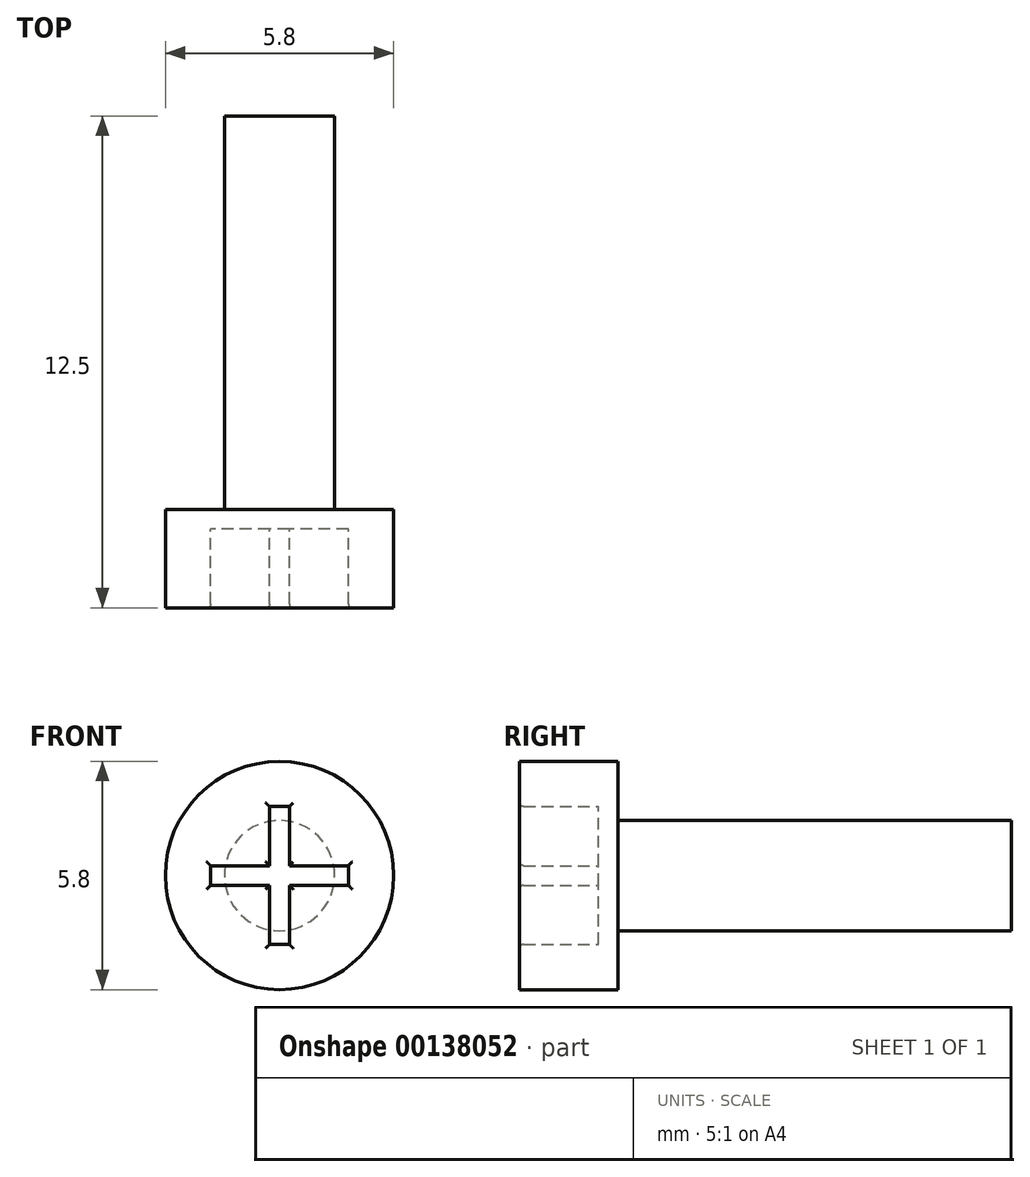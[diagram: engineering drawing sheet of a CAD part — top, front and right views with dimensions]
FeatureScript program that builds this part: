
annotation { "Feature Type Name" : "Feature", "Feature Type Description" : "" }
export const myFeature = defineFeature(function(context is Context, id is Id, definition is map)
    precondition{}
    {
        {
            var Q0;
            Q0=qCreatedBy(makeId("Front.planeOp"),FACE);
            var sketch = newSketch(context, id + "F0", { "sketchPlane" : qUnion([Q0])});
            skCircle(sketch, "E0", {"center": v(0, 0) * mm, "radius": 1.4 * mm});
            skSolve(sketch);
        }
        {
            var Q0;
            Q0=makeQuery(id+"F0.imprint","IMPRINT",FACE,{"disambiguationData":[TD([[makeQuery(id+"F0.imprint","IMPRINT",EDGE,{"derivedFrom":sQuery(id+"F0.wireOp",EDGE,"E0")}),1.0]])]});
            extrude(context, id + "F1", {"entities" : qUnion([Q0]), "depth" : 10 * mm});
        }
        {
            var Q0;
            Q0=makeQuery(id+"F1.opExtrude","CAP_FACE",FACE,{"disambiguationData":[OSD([sQuery(id+"F0.wireOp",EDGE,"E0")])],"isStart":false});
            cPlane(context, id + "F2", {"entities" : qUnion([Q0]), "cplaneType" : CPlaneType.OFFSET, "offset" : 0 * mm, "width" : 150 * mm, "height" : 150 * mm});
        }
        {
            var Q0;
            Q0=qCreatedBy(id+"F2.planeOp",FACE);
            var sketch = newSketch(context, id + "F3", { "sketchPlane" : qUnion([Q0])});
            skCircle(sketch, "E1", {"center": v(0, 0) * mm, "radius": 2.9 * mm});
            skLineSegment(sketch, "E2.bottom", {"start": v(0.25, -1.75) * mm, "end": v(-0.25, -1.75) * mm});
            skLineSegment(sketch, "E2.top", {"start": v(0.25, 1.75) * mm, "end": v(-0.25, 1.75) * mm});
            skLineSegment(sketch, "E2.left", {"start": v(0.25, -1.75) * mm, "end": v(0.25, 1.75) * mm});
            skLineSegment(sketch, "E2.right", {"start": v(-0.25, -1.75) * mm, "end": v(-0.25, 1.75) * mm});
            skLineSegment(sketch, "E3.bottom", {"start": v(1.75, -0.25) * mm, "end": v(-1.75, -0.25) * mm});
            skLineSegment(sketch, "E3.top", {"start": v(1.75, 0.25) * mm, "end": v(-1.75, 0.25) * mm});
            skLineSegment(sketch, "E3.left", {"start": v(1.75, -0.25) * mm, "end": v(1.75, 0.25) * mm});
            skLineSegment(sketch, "E3.right", {"start": v(-1.75, -0.25) * mm, "end": v(-1.75, 0.25) * mm});
            skSolve(sketch);
        }
        {
            var Q0;
            Q0=makeQuery(id+"F3.imprint","IMPRINT",FACE,{"disambiguationData":[TD([[makeQuery(id+"F3.imprint","IMPRINT",EDGE,{"derivedFrom":sQuery(id+"F3.wireOp",EDGE,"E1")}),1.0]])]});
            extrude(context, id + "F4", {"entities" : qUnion([Q0]), "operationType" : NewBodyOperationType.ADD, "depth" : 2.5 * mm});
        }
        {
            var Q0;
            {var subQ0=sQuery(id+"F3.wireOp",EDGE,"E3.bottom");var subQ1=sQuery(id+"F3.wireOp",EDGE,"E2.left");var subQ2=makeQuery(id+"F3.imprint","INTERSECT",VERTEX,{"derivedFrom":[subQ1,subQ0]});Q0=makeQuery(id+"F3.imprint","IMPRINT",FACE,{"disambiguationData":[TD([[makeQuery(id+"F3.imprint","IMPRINT",EDGE,{"disambiguationData":[TD([[subQ2,-1.0]])],"derivedFrom":subQ1}),1.0]])]});}
            var Q1;
            {var subQ5=sQuery(id+"F3.wireOp",EDGE,"E3.right");Q1=makeQuery(id+"F3.imprint","IMPRINT",FACE,{"disambiguationData":[TD([[makeQuery(id+"F3.imprint","IMPRINT",EDGE,{"derivedFrom":subQ5}),-1.0]])]});}
            var Q2;
            {var subQ0=sQuery(id+"F3.wireOp",EDGE,"E2.bottom");Q2=makeQuery(id+"F3.imprint","IMPRINT",FACE,{"disambiguationData":[TD([[makeQuery(id+"F3.imprint","IMPRINT",EDGE,{"derivedFrom":subQ0}),-1.0]])]});}
            var Q3;
            {var subQ5=sQuery(id+"F3.wireOp",EDGE,"E3.left");Q3=makeQuery(id+"F3.imprint","IMPRINT",FACE,{"disambiguationData":[TD([[makeQuery(id+"F3.imprint","IMPRINT",EDGE,{"derivedFrom":subQ5}),1.0]])]});}
            var Q4;
            {var subQ0=sQuery(id+"F3.wireOp",EDGE,"E2.top");Q4=makeQuery(id+"F3.imprint","IMPRINT",FACE,{"disambiguationData":[TD([[makeQuery(id+"F3.imprint","IMPRINT",EDGE,{"derivedFrom":subQ0}),1.0]])]});}
            extrude(context, id + "F5", {"entities" : qUnion([Q0, Q1, Q2, Q3, Q4]), "operationType" : NewBodyOperationType.ADD, "depth" : 0.5 * mm});
        }
        {
            var Q0;
            {var subQ0=sQuery(id+"F3.wireOp",EDGE,"E2.right");Q0=makeQuery(id+"F4.opExtrude","CAP_EDGE",EDGE,{"disambiguationData":[OSD([subQ0]),TDD([makeQuery(id+"F3.imprint","IMPRINT",EDGE,{"disambiguationData":[TD([[makeQuery(id+"F3.imprint","INTERSECT",VERTEX,{"derivedFrom":[sQuery(id+"F3.wireOp",EDGE,"E2.top"),subQ0]}),1.0]])],"derivedFrom":subQ0})])],"isStart":false});}
            var Q1;
            {var subQ0=sQuery(id+"F3.wireOp",EDGE,"E3.top");Q1=makeQuery(id+"F4.opExtrude","CAP_EDGE",EDGE,{"disambiguationData":[OSD([subQ0]),TDD([makeQuery(id+"F3.imprint","IMPRINT",EDGE,{"disambiguationData":[TD([[makeQuery(id+"F3.imprint","INTERSECT",VERTEX,{"derivedFrom":[subQ0,sQuery(id+"F3.wireOp",EDGE,"E3.right")]}),1.0]])],"derivedFrom":subQ0})])],"isStart":false});}
            var Q2;
            {var subQ0=sQuery(id+"F3.wireOp",EDGE,"E3.bottom");Q2=makeQuery(id+"F4.opExtrude","CAP_EDGE",EDGE,{"disambiguationData":[OSD([subQ0]),TDD([makeQuery(id+"F3.imprint","IMPRINT",EDGE,{"disambiguationData":[TD([[makeQuery(id+"F3.imprint","INTERSECT",VERTEX,{"derivedFrom":[subQ0,sQuery(id+"F3.wireOp",EDGE,"E3.right")]}),1.0]])],"derivedFrom":subQ0})])],"isStart":false});}
            var Q3;
            {var subQ0=sQuery(id+"F3.wireOp",EDGE,"E2.right");Q3=makeQuery(id+"F4.opExtrude","CAP_EDGE",EDGE,{"disambiguationData":[OSD([subQ0]),TDD([makeQuery(id+"F3.imprint","IMPRINT",EDGE,{"disambiguationData":[TD([[makeQuery(id+"F3.imprint","INTERSECT",VERTEX,{"derivedFrom":[sQuery(id+"F3.wireOp",EDGE,"E2.bottom"),subQ0]}),-1.0]])],"derivedFrom":subQ0})])],"isStart":false});}
            var Q4;
            Q4=makeQuery(id+"F4.opExtrude","CAP_EDGE",EDGE,{"disambiguationData":[OSD([sQuery(id+"F3.wireOp",EDGE,"E3.right")])],"isStart":false});
            var Q5;
            {var subQ0=sQuery(id+"F3.wireOp",EDGE,"E2.left");Q5=makeQuery(id+"F4.opExtrude","CAP_EDGE",EDGE,{"disambiguationData":[OSD([subQ0]),TDD([makeQuery(id+"F3.imprint","IMPRINT",EDGE,{"disambiguationData":[TD([[makeQuery(id+"F3.imprint","INTERSECT",VERTEX,{"derivedFrom":[sQuery(id+"F3.wireOp",EDGE,"E2.bottom"),subQ0]}),-1.0]])],"derivedFrom":subQ0})])],"isStart":false});}
            var Q6;
            Q6=makeQuery(id+"F4.opExtrude","CAP_EDGE",EDGE,{"disambiguationData":[OSD([sQuery(id+"F3.wireOp",EDGE,"E2.bottom")])],"isStart":false});
            var Q7;
            {var subQ0=sQuery(id+"F3.wireOp",EDGE,"E3.bottom");Q7=makeQuery(id+"F4.opExtrude","CAP_EDGE",EDGE,{"disambiguationData":[OSD([subQ0]),TDD([makeQuery(id+"F3.imprint","IMPRINT",EDGE,{"disambiguationData":[TD([[makeQuery(id+"F3.imprint","INTERSECT",VERTEX,{"derivedFrom":[subQ0,sQuery(id+"F3.wireOp",EDGE,"E3.left")]}),-1.0]])],"derivedFrom":subQ0})])],"isStart":false});}
            var Q8;
            Q8=makeQuery(id+"F4.opExtrude","CAP_EDGE",EDGE,{"disambiguationData":[OSD([sQuery(id+"F3.wireOp",EDGE,"E3.left")])],"isStart":false});
            var Q9;
            {var subQ0=sQuery(id+"F3.wireOp",EDGE,"E2.left");Q9=makeQuery(id+"F4.opExtrude","CAP_EDGE",EDGE,{"disambiguationData":[OSD([subQ0]),TDD([makeQuery(id+"F3.imprint","IMPRINT",EDGE,{"disambiguationData":[TD([[makeQuery(id+"F3.imprint","INTERSECT",VERTEX,{"derivedFrom":[sQuery(id+"F3.wireOp",EDGE,"E2.top"),subQ0]}),1.0]])],"derivedFrom":subQ0})])],"isStart":false});}
            var Q10;
            Q10=makeQuery(id+"F4.opExtrude","CAP_EDGE",EDGE,{"disambiguationData":[OSD([sQuery(id+"F3.wireOp",EDGE,"E2.top")])],"isStart":false});
            var Q11;
            {var subQ0=sQuery(id+"F3.wireOp",EDGE,"E3.top");Q11=makeQuery(id+"F4.opExtrude","CAP_EDGE",EDGE,{"disambiguationData":[OSD([subQ0]),TDD([makeQuery(id+"F3.imprint","IMPRINT",EDGE,{"disambiguationData":[TD([[makeQuery(id+"F3.imprint","INTERSECT",VERTEX,{"derivedFrom":[subQ0,sQuery(id+"F3.wireOp",EDGE,"E3.left")]}),-1.0]])],"derivedFrom":subQ0})])],"isStart":false});}
            fillet(context, id + "F6", {"entities" : qUnion([Q0, Q1, Q2, Q3, Q4, Q5, Q6, Q7, Q8, Q9, Q10, Q11]), "radius" : 0.1 * mm, "tangentPropagation" : true, "allowEdgeOverflow" : false});
        }
    });
